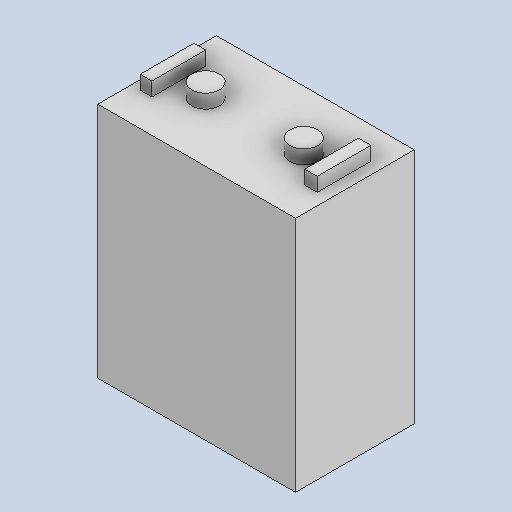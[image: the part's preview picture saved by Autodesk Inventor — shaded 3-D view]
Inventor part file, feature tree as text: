
AUTODESK INVENTOR PART (.ipt)
format: ipt  version: 2023 (Build 270158000, 158)  size: 225,280 bytes
history: native  units: mm
features: sketch x4, extrude x3
ambient origin geometry x8: Origin, YZ Plane, XZ Plane, XY Plane, X Axis, Y Axis, Z Axis, Center Point
bodies: Solid1 (feature_tree)
feature tree (7):
  sketch  "Sketch1"  dims[d0=50.0mm d1=60.0mm]
  extrude  "Extrusion1"  Depth=60.0mm
  extrude  "Extrusion2"  Depth=3.5mm TaperAngle=0.0deg
  extrude  "Extrusion3"  Depth=7.0mm
  sketch  "Sketch2"  dims[d2=30.0mm d3=0.0mm d4=3.5mm d5=0.0mm]
  sketch  "Sketch3"  dims[d6=15.0mm d7=7.0mm]
  sketch  "Sketch4"  dims[d8=7.0mm d9=7.0mm d10=24.628115mm d11=7.0mm d12=3.5mm d13=0.0mm]
